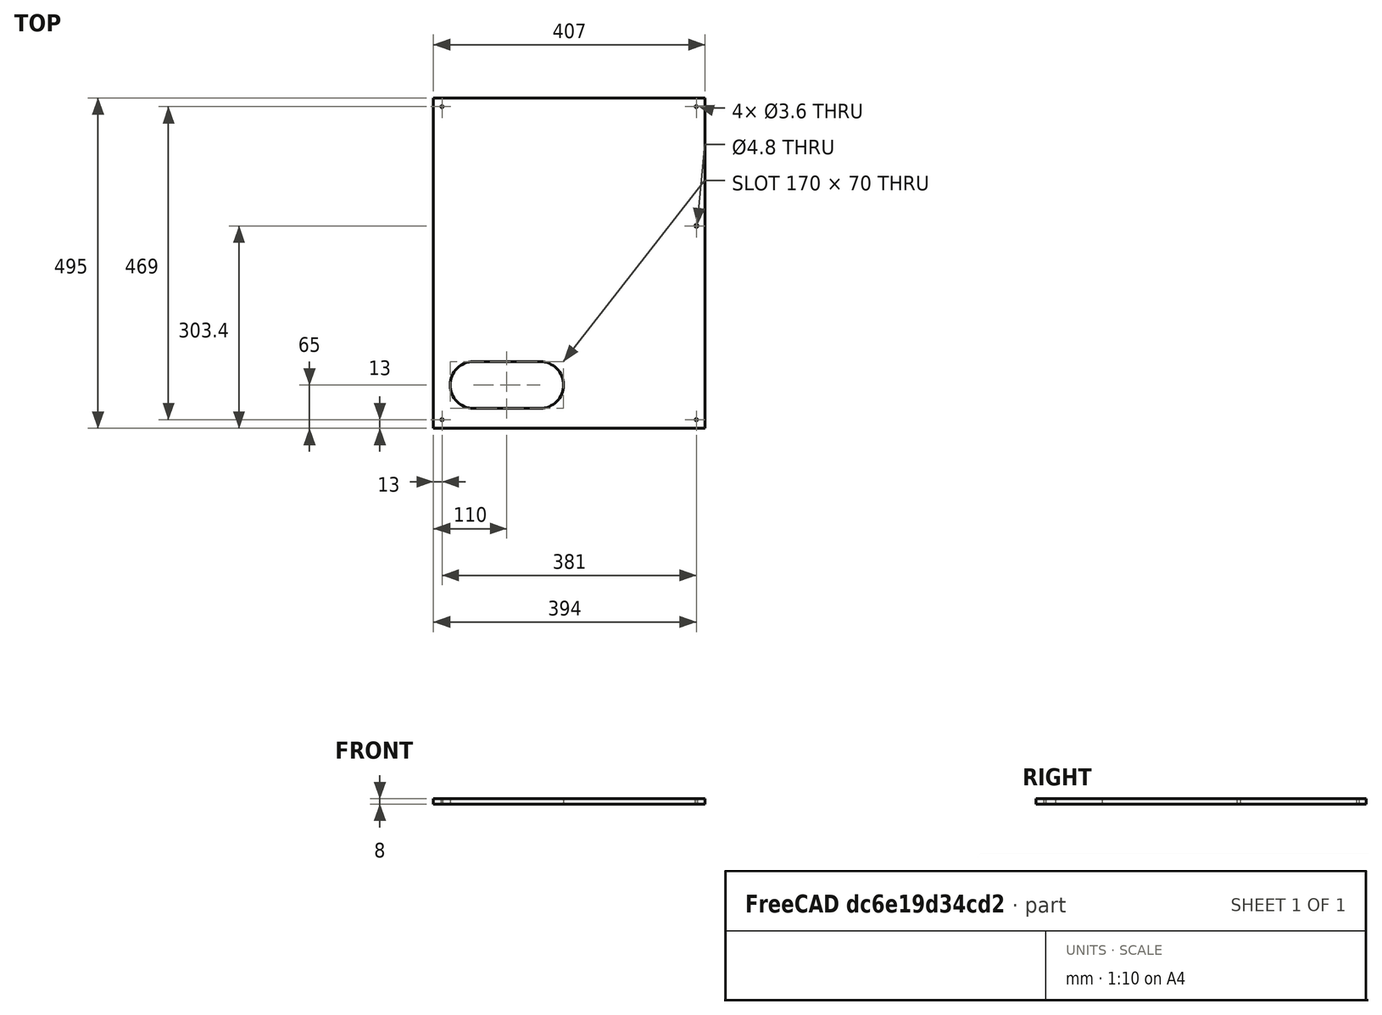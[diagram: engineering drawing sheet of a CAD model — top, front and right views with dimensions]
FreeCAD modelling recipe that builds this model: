
FCSTD DOCUMENT  (FreeCAD 0.16R6706 (Git))
Label: Lado Direito
License: All rights reserved
LicenseURL: http://en.wikipedia.org/wiki/All_rights_reserved
objects: Path::FeaturePython×9, Sketcher::SketchObject×1, PartDesign::Pad×1, Path::FeatureCompoundPython×1
note: 3 computed .brp shape members not serialized (recipe doc carries the construction recipe); baked Part::Feature solids carry a one-line shape summary decoded from their .brp

FEATURE [Sketcher::SketchObject] Sketch
  sketch-geometry (17):
    g0: LineSegment StartX=-203.5 StartY=247.5 StartZ=0 EndX=203.5 EndY=247.5 EndZ=0
    g1: LineSegment StartX=203.5 StartY=247.5 StartZ=0 EndX=203.5 EndY=-247.5 EndZ=0
    g2: LineSegment StartX=203.5 StartY=-247.5 StartZ=0 EndX=-203.5 EndY=-247.5 EndZ=0
    g3: LineSegment StartX=-203.5 StartY=-247.5 StartZ=0 EndX=-203.5 EndY=247.5 EndZ=0
    g4: LineSegment [constr] StartX=-190.5 StartY=234.5 StartZ=0 EndX=190.5 EndY=234.5 EndZ=0
    g5: LineSegment [constr] StartX=190.5 StartY=234.5 StartZ=0 EndX=190.5 EndY=-234.5 EndZ=0
    g6: LineSegment [constr] StartX=190.5 StartY=-234.5 StartZ=0 EndX=-190.5 EndY=-234.5 EndZ=0
    g7: LineSegment [constr] StartX=-190.5 StartY=-234.5 StartZ=0 EndX=-190.5 EndY=234.5 EndZ=0
    g8: Circle CenterX=-190.5 CenterY=234.5 CenterZ=0 NormalX=0 NormalY=0 NormalZ=1 Radius=1.8
    g9: Circle CenterX=190.5 CenterY=234.5 CenterZ=0 NormalX=0 NormalY=0 NormalZ=1 Radius=1.8
    g10: Circle CenterX=-190.5 CenterY=-234.5 CenterZ=0 NormalX=0 NormalY=0 NormalZ=1 Radius=1.8
    g11: Circle CenterX=190.5 CenterY=-234.5 CenterZ=0 NormalX=0 NormalY=0 NormalZ=1 Radius=1.8
    g12: Circle CenterX=190.5 CenterY=55.9 CenterZ=0 NormalX=0 NormalY=0 NormalZ=1 Radius=2.4
    g13: ArcOfCircle CenterX=-143.5 CenterY=-182.5 CenterZ=0 NormalX=0 NormalY=0 NormalZ=1 Radius=35 StartAngle=1.5708 EndAngle=4.71239
    g14: ArcOfCircle CenterX=-43.5 CenterY=-182.5 CenterZ=0 NormalX=0 NormalY=0 NormalZ=1 Radius=35 StartAngle=4.71239 EndAngle=7.85398
    g15: LineSegment StartX=-143.5 StartY=-217.5 StartZ=0 EndX=-43.5 EndY=-217.5 EndZ=0
    g16: LineSegment StartX=-143.5 StartY=-147.5 StartZ=0 EndX=-43.5 EndY=-147.5 EndZ=0
  constraints (43):
    c: Coincident(g0,g1)
    c: Coincident(g1,g2)
    c: Coincident(g2,g3)
    c: Coincident(g3,g0)
    c: Horizontal(g0)
    c: Horizontal(g2)
    c: Vertical(g1)
    c: Vertical(g3)
    c: Symmetric(g2,g0,g-1)
    c: Coincident(g4,g5)
    c: Coincident(g5,g6)
    c: Coincident(g6,g7)
    c: Coincident(g7,g4)
    c: Horizontal(g4)
    c: Horizontal(g6)
    c: Vertical(g5)
    c: Vertical(g7)
    c: Symmetric(g4,g6,g-1)
    c: DistanceX(g0,g4) = 13
    c: DistanceY(g4,g0) = 13
    c: DistanceX(g0,g0) = 407
    c: DistanceY(g1,g1) = 495
    c: Radius(g8) = 1.8
    c: Equal(g8,g9) = 1.8
    c: Equal(g8,g10) = 1.8
    c: Equal(g8,g11) = 1.8
    c: Coincident(g4,g8)
    c: Coincident(g10,g6)
    c: Coincident(g11,g5)
    c: Coincident(g4,g9)
    c: Radius(g12) = 2.4
    c: DistanceY(g12,g0) = 191.6
    c: PointOnObject(g12,g5)
    c: Tangent(g13,g16) = 1.5708
    c: Tangent(g13,g15) = -1.5708
    c: Tangent(g15,g14) = -1.5708
    c: Tangent(g16,g14) = 1.5708
    c: Horizontal(g15)
    c: Equal(g13,g14)
    c: DistanceY(g14,g14) = 70
    c: DistanceY(g2,g13) = 30
    c: DistanceX(g2,g13) = 60
    c: DistanceX(g16,g16) = 100
FEATURE [PartDesign::Pad] Pad
  Length = 8
  Length2 = 100
  Sketch = -> Sketch
  Type = 0
FEATURE [Path::FeaturePython] Machine  label="Machine_"  # Path/CAM operation (typed FeaturePython)
  MachineUnits = 0
  X = 0
  X_Max = 0
  X_Min = 0
  Y = 0
  Y_Max = 0
  Y_Min = 0
  Z = 0
  Z_Max = 0
  Z_Min = 0
FEATURE [Path::FeaturePython] Tool  label="Tool1"  # Path/CAM operation (typed FeaturePython)
  SpindleDir = 0
  SpindleSpeed = 0
  ToolNumber = 1
FEATURE [Path::FeaturePython] Profile  label="Cantoneira"  # Path/CAM operation (typed FeaturePython)
  Active = true
  Base = -> Pad
  ClearanceHeight = 3
  Direction = 1
  Edge1 = -> Pad [Edge33]
  EndPoint = (0,0,0)
  ExtendAtEnd = 0
  ExtendAtStart = 0
  FinalDepth = -8.1
  HorizFeed = 127
  LeadInLineLen = 0
  LeadOutLineLen = 0
  OffsetExtra = 0
  PathClosed = true
  RetractHeight = 0
  RollRadius = 0
  SegLen = 0.5
  Side = 1
  StartDepth = 0
  StartPoint = (0,0,0)
  StepDown = 3
  ToolNumber = 1
  UseEndPoint = false
  UsePlacements = false
  UseStartDepth = true
  UseStartPoint = false
  VertFeed = 127
FEATURE [Path::FeaturePython] Profile001  label="Cantoneira001"  # Path/CAM operation (typed FeaturePython)
  Active = true
  Base = -> Pad
  ClearanceHeight = 3
  Direction = 1
  Edge1 = -> Pad [Edge39]
  EndPoint = (0,0,0)
  ExtendAtEnd = 0
  ExtendAtStart = 0
  FinalDepth = -8.1
  HorizFeed = 127
  LeadInLineLen = 0
  LeadOutLineLen = 0
  OffsetExtra = 0
  PathClosed = true
  RetractHeight = 0
  RollRadius = 0
  SegLen = 0.5
  Side = 1
  StartDepth = 0
  StartPoint = (0,0,0)
  StepDown = 3
  ToolNumber = 1
  UseEndPoint = false
  UsePlacements = false
  UseStartDepth = true
  UseStartPoint = false
  VertFeed = 127
FEATURE [Path::FeaturePython] Profile002  label="Cantoneira002"  # Path/CAM operation (typed FeaturePython)
  Active = true
  Base = -> Pad
  ClearanceHeight = 3
  Direction = 1
  Edge1 = -> Pad [Edge36]
  EndPoint = (0,0,0)
  ExtendAtEnd = 0
  ExtendAtStart = 0
  FinalDepth = -8.1
  HorizFeed = 127
  LeadInLineLen = 0
  LeadOutLineLen = 0
  OffsetExtra = 0
  PathClosed = true
  RetractHeight = 0
  RollRadius = 0
  SegLen = 0.5
  Side = 1
  StartDepth = 0
  StartPoint = (0,0,0)
  StepDown = 3
  ToolNumber = 1
  UseEndPoint = false
  UsePlacements = false
  UseStartDepth = true
  UseStartPoint = false
  VertFeed = 127
FEATURE [Path::FeaturePython] Profile003  label="Cantoneira003"  # Path/CAM operation (typed FeaturePython)
  Active = true
  Base = -> Pad
  ClearanceHeight = 3
  Direction = 1
  Edge1 = -> Pad [Edge27]
  EndPoint = (0,0,0)
  ExtendAtEnd = 0
  ExtendAtStart = 0
  FinalDepth = -8.1
  HorizFeed = 127
  LeadInLineLen = 0
  LeadOutLineLen = 0
  OffsetExtra = 0
  PathClosed = true
  RetractHeight = 0
  RollRadius = 0
  SegLen = 0.5
  Side = 1
  StartDepth = 0
  StartPoint = (0,0,0)
  StepDown = 3
  ToolNumber = 1
  UseEndPoint = false
  UsePlacements = false
  UseStartDepth = true
  UseStartPoint = false
  VertFeed = 127
FEATURE [Path::FeaturePython] Profile004  label="Cantoneira004"  # Path/CAM operation (typed FeaturePython)
  Active = true
  Base = -> Pad
  ClearanceHeight = 3
  Direction = 1
  Edge1 = -> Pad [Edge30]
  EndPoint = (0,0,0)
  ExtendAtEnd = 0
  ExtendAtStart = 0
  FinalDepth = -8.1
  HorizFeed = 127
  LeadInLineLen = 0
  LeadOutLineLen = 0
  OffsetExtra = 0
  PathClosed = true
  RetractHeight = 0
  RollRadius = 0
  SegLen = 0.5
  Side = 1
  StartDepth = 0
  StartPoint = (0,0,0)
  StepDown = 3
  ToolNumber = 1
  UseEndPoint = false
  UsePlacements = false
  UseStartDepth = true
  UseStartPoint = false
  VertFeed = 127
FEATURE [Path::FeaturePython] Profile005  label="Janela"  # Path/CAM operation (typed FeaturePython)
  Active = true
  Base = -> Pad
  ClearanceHeight = 3
  Direction = 1
  Edge1 = -> Pad [Edge16]
  Edge2 = -> Pad [Edge19]
  EndPoint = (0,0,0)
  ExtendAtEnd = 0
  ExtendAtStart = 0
  FinalDepth = -8.1
  HorizFeed = 127
  LeadInLineLen = 0
  LeadOutLineLen = 0
  OffsetExtra = 0
  PathClosed = true
  RetractHeight = 0
  RollRadius = 0
  SegLen = 0.5
  Side = 1
  StartDepth = 0
  StartPoint = (0,0,0)
  StepDown = 3
  ToolNumber = 1
  UseEndPoint = false
  UsePlacements = false
  UseStartDepth = true
  UseStartPoint = false
  VertFeed = 127
FEATURE [Path::FeaturePython] Profile006  label="Externo"  # Path/CAM operation (typed FeaturePython)
  Active = true
  Base = -> Pad
  ClearanceHeight = 3
  Direction = 0
  EndPoint = (0,0,0)
  ExtendAtEnd = 0
  ExtendAtStart = 0
  Face1 = -> Pad [Face15]
  FinalDepth = -8.1
  HorizFeed = 127
  LeadInLineLen = 0
  LeadOutLineLen = 0
  OffsetExtra = 0
  PathClosed = true
  RetractHeight = 0
  RollRadius = 0
  SegLen = 0.5
  Side = 0
  StartDepth = 0
  StartPoint = (0,0,0)
  StepDown = 3
  ToolNumber = 1
  UseEndPoint = false
  UsePlacements = false
  UseStartDepth = true
  UseStartPoint = false
  VertFeed = 127
FEATURE [Path::FeatureCompoundPython] Project  # Path/CAM operation (typed FeaturePython)
  Group = -> [Machine,Tool,Profile,Profile001,Profile002,Profile003,Profile004,Profile005,Profile006]
  UsePlacements = false
